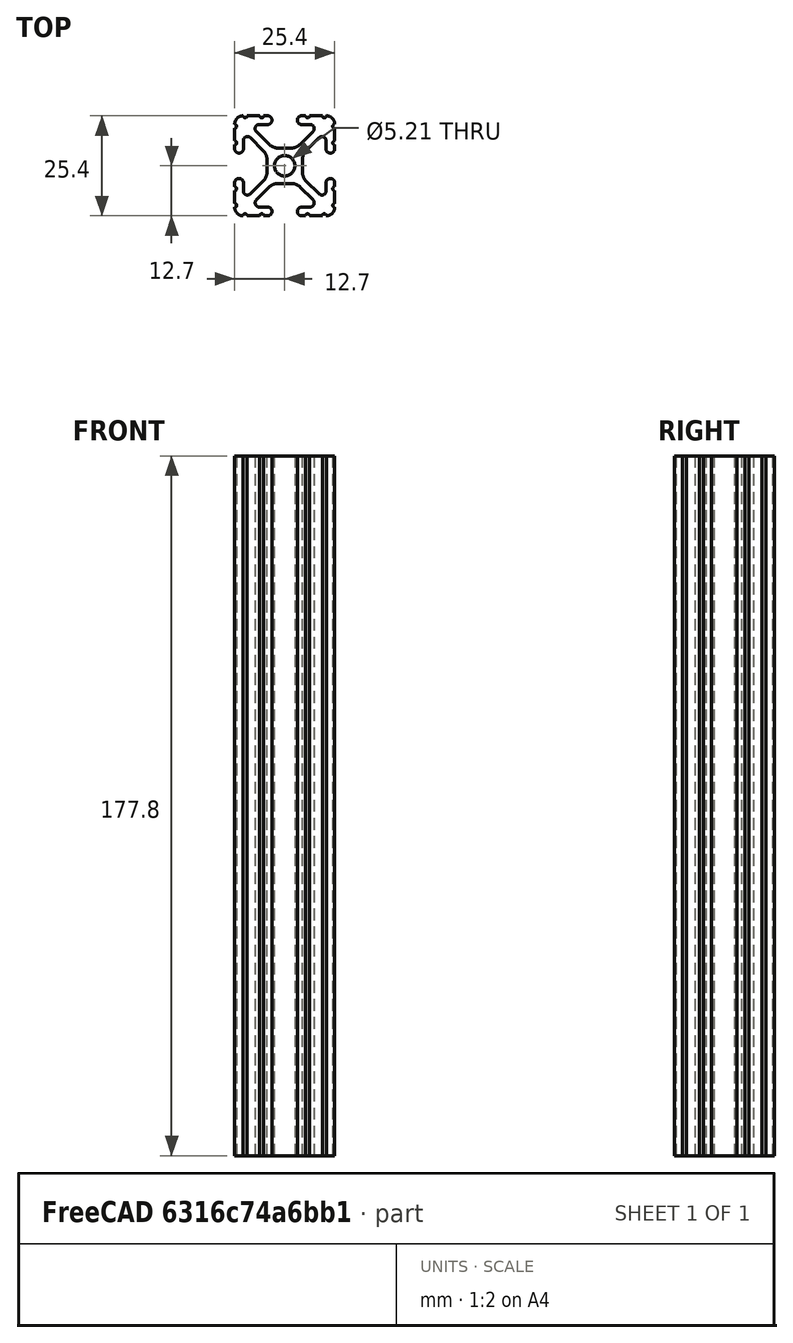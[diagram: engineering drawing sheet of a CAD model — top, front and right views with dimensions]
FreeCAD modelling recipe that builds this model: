
FCSTD DOCUMENT  (FreeCAD 0.19R23756 (Git))
Label: 1010-7
License: All rights reserved
LicenseURL: http://en.wikipedia.org/wiki/All_rights_reserved
objects: Sketcher::SketchObject×1, Part::Extrusion×1
note: 2 computed .brp shape members not serialized (recipe doc carries the construction recipe); baked Part::Feature solids carry a one-line shape summary decoded from their .brp

FEATURE [Sketcher::SketchObject] Sketch097
  FullyConstrained = false
  sketch-geometry (97):
    g0: Circle CenterX=0 CenterY=0 CenterZ=0 NormalX=0 NormalY=0 NormalZ=-1 AngleXU=0 Radius=2.6035
    g1: ArcOfCircle CenterX=12.7 CenterY=5.82508 CenterZ=0 NormalX=0 NormalY=0 NormalZ=1 AngleXU=0 Radius=0.508 StartAngle=1.5708 EndAngle=4.71239
    g2: LineSegment StartX=3.2385 StartY=11.651 StartZ=0 EndX=3.2385 EndY=11.5392 EndZ=0
    g3: LineSegment StartX=6.33313 StartY=-12.7 StartZ=0 EndX=9.55044 EndY=-12.7 EndZ=0
    g4: LineSegment StartX=7.20704 StartY=8.72437 StartZ=0 EndX=3.89827 EndY=5.42317 EndZ=0
    g5: ArcOfCircle CenterX=7.6835 CenterY=1.59319 CenterZ=0 NormalX=0 NormalY=0 NormalZ=1 AngleXU=0 Radius=3.175 StartAngle=2.35505 EndAngle=3.14159
    g6: ArcOfCircle CenterX=-1.70925 CenterY=-7.6708 CenterZ=0 NormalX=0 NormalY=0 NormalZ=1 AngleXU=0 Radius=3.175 StartAngle=1.5708 EndAngle=2.35528
    g7: ArcOfCircle CenterX=11.5392 CenterY=-4.28747 CenterZ=0 NormalX=0 NormalY=0 NormalZ=1 AngleXU=0 Radius=1.04901 StartAngle=1.5708 EndAngle=3.14159
    g8: ArcOfCircle CenterX=12.7 CenterY=-5.82508 CenterZ=0 NormalX=0 NormalY=0 NormalZ=1 AngleXU=0 Radius=0.508 StartAngle=1.5708 EndAngle=4.71239
    g9: LineSegment StartX=4.28751 StartY=10.4902 StartZ=0 EndX=6.47679 EndY=10.4902 EndZ=0
    g10: ArcOfCircle CenterX=4.28751 CenterY=11.651 CenterZ=0 NormalX=0 NormalY=0 NormalZ=1 AngleXU=0 Radius=1.04901 StartAngle=1.5708 EndAngle=3.14159
    g11: ArcOfCircle CenterX=6.47679 CenterY=9.45629 CenterZ=0 NormalX=0 NormalY=0 NormalZ=1 AngleXU=0 Radius=1.03391 StartAngle=5.49664 EndAngle=7.85398
    g12: ArcOfCircle CenterX=4.28751 CenterY=11.5392 CenterZ=0 NormalX=0 NormalY=0 NormalZ=1 AngleXU=0 Radius=1.04901 StartAngle=3.14159 EndAngle=4.71239
    g13: LineSegment StartX=3.95227 StartY=-5.42369 StartZ=0 EndX=7.17965 EndY=-8.64519 EndZ=0
    g14: ArcOfCircle CenterX=11.651 CenterY=4.28747 CenterZ=0 NormalX=0 NormalY=0 NormalZ=1 AngleXU=0 Radius=1.04901 StartAngle=4.71239 EndAngle=6.28319
    g15: ArcOfCircle CenterX=-5.82513 CenterY=-12.7 CenterZ=0 NormalX=0 NormalY=0 NormalZ=1 AngleXU=0 Radius=0.508 StartAngle=0 EndAngle=3.14159
    g16: LineSegment StartX=-6.47679 StartY=10.4902 StartZ=0 EndX=-4.28751 EndY=10.4902 EndZ=0
    g17: ArcOfCircle CenterX=-12.7 CenterY=10.0584 CenterZ=0 NormalX=0 NormalY=0 NormalZ=1 AngleXU=0 Radius=0.508 StartAngle=4.71239 EndAngle=7.85368
    g18: ArcOfCircle CenterX=-12.7 CenterY=5.82508 CenterZ=0 NormalX=0 NormalY=0 NormalZ=1 AngleXU=0 Radius=0.508 StartAngle=4.71239 EndAngle=7.85398
    g19: LineSegment StartX=-11.5392 StartY=-3.23846 StartZ=0 EndX=-11.651 EndY=-3.23846 EndZ=0
    g20: LineSegment StartX=-3.89827 StartY=5.42317 StartZ=0 EndX=-7.20704 EndY=8.72437 EndZ=0
    g21: LineSegment StartX=1.65578 StartY=4.4958 StartZ=0 EndX=-1.65578 EndY=4.4958 EndZ=0
    g22: ArcOfCircle CenterX=-1.65578 CenterY=7.6708 CenterZ=0 NormalX=0 NormalY=0 NormalZ=1 AngleXU=0 Radius=3.175 StartAngle=3.92813 EndAngle=4.71239
    g23: LineSegment StartX=-9.55044 StartY=-12.7 StartZ=0 EndX=-6.33313 EndY=-12.7 EndZ=0
    g24: ArcOfCircle CenterX=-5.82513 CenterY=12.7 CenterZ=0 NormalX=0 NormalY=0 NormalZ=1 AngleXU=0 Radius=0.508 StartAngle=3.14159 EndAngle=6.28319
    g25: ArcOfCircle CenterX=-4.28751 CenterY=11.651 CenterZ=0 NormalX=0 NormalY=0 NormalZ=1 AngleXU=0 Radius=1.04901 StartAngle=0 EndAngle=1.5708
    g26: LineSegment StartX=-12.7 StartY=-4.28747 StartZ=0 EndX=-12.7 EndY=-5.31708 EndZ=0
    g27: ArcOfCircle CenterX=-6.47679 CenterY=9.45629 CenterZ=0 NormalX=0 NormalY=0 NormalZ=1 AngleXU=0 Radius=1.03391 StartAngle=1.5708 EndAngle=3.92813
    g28: ArcOfCircle CenterX=-4.28751 CenterY=11.5392 CenterZ=0 NormalX=0 NormalY=0 NormalZ=1 AngleXU=0 Radius=1.04901 StartAngle=4.71239 EndAngle=6.28319
    g29: LineSegment StartX=-5.44101 StartY=-3.84082 StartZ=0 EndX=-8.73713 EndY=-7.12941 EndZ=0
    g30: ArcOfCircle CenterX=-7.6835 CenterY=-1.59319 CenterZ=0 NormalX=0 NormalY=0 NormalZ=1 AngleXU=0 Radius=3.175 StartAngle=5.49664 EndAngle=6.28319
    g31: LineSegment StartX=-12.7 StartY=5.31708 StartZ=0 EndX=-12.7 EndY=4.28747 EndZ=0
    g32: LineSegment StartX=-8.73713 StartY=7.12941 StartZ=0 EndX=-5.44101 EndY=3.84082 EndZ=0
    g33: LineSegment StartX=-11.651 StartY=3.23846 StartZ=0 EndX=-11.5392 EndY=3.23846 EndZ=0
    g34: ArcOfCircle CenterX=-9.46279 CenterY=-6.40209 CenterZ=0 NormalX=0 NormalY=0 NormalZ=1 AngleXU=0 Radius=1.02741 StartAngle=3.14159 EndAngle=5.49664
    g35: ArcOfCircle CenterX=-10.5918 CenterY=10.5918 CenterZ=0 NormalX=0 NormalY=0 NormalZ=1 AngleXU=0 Radius=2.1082 StartAngle=1.55877 EndAngle=3.15364
    g36: LineSegment StartX=-12.7 StartY=9.5504 StartZ=0 EndX=-12.7 EndY=6.33308 EndZ=0
    g37: LineSegment StartX=-6.33313 StartY=12.7 StartZ=0 EndX=-9.55044 EndY=12.7 EndZ=0
    g38: ArcOfCircle CenterX=-11.5392 CenterY=-4.28747 CenterZ=0 NormalX=0 NormalY=0 NormalZ=1 AngleXU=0 Radius=1.04901 StartAngle=0 EndAngle=1.5708
    g39: LineSegment StartX=4.28751 StartY=-12.7 StartZ=0 EndX=5.31713 EndY=-12.7 EndZ=0
    g40: LineSegment StartX=5.44101 StartY=3.84082 StartZ=0 EndX=8.73713 EndY=7.12941 EndZ=0
    g41: LineSegment StartX=10.4902 StartY=-4.28747 StartZ=0 EndX=10.4902 EndY=-6.40209 EndZ=0
    g42: ArcOfCircle CenterX=9.46279 CenterY=6.40209 CenterZ=0 NormalX=0 NormalY=0 NormalZ=1 AngleXU=0 Radius=1.02741 StartAngle=0 EndAngle=2.35505
    g43: ArcOfCircle CenterX=5.82513 CenterY=-12.7 CenterZ=0 NormalX=0 NormalY=0 NormalZ=1 AngleXU=0 Radius=0.508 StartAngle=0 EndAngle=3.14159
    g44: LineSegment StartX=12.7 StartY=-9.5504 StartZ=0 EndX=12.7 EndY=-6.33308 EndZ=0
    g45: LineSegment StartX=4.5085 StartY=-1.59319 StartZ=0 EndX=4.5085 EndY=1.59319 EndZ=0
    g46: ArcOfCircle CenterX=12.7 CenterY=10.0584 CenterZ=0 NormalX=0 NormalY=0 NormalZ=1 AngleXU=0 Radius=0.508 StartAngle=1.5711 EndAngle=4.71239
    g47: ArcOfCircle CenterX=12.7 CenterY=-10.0584 CenterZ=0 NormalX=0 NormalY=0 NormalZ=1 AngleXU=0 Radius=0.508 StartAngle=1.5708 EndAngle=4.71209
    g48: LineSegment StartX=3.2385 StartY=-11.5392 StartZ=0 EndX=3.2385 EndY=-11.651 EndZ=0
    g49: LineSegment StartX=8.73713 StartY=-7.12941 StartZ=0 EndX=5.44101 EndY=-3.84082 EndZ=0
    g50: ArcOfCircle CenterX=11.651 CenterY=-4.28747 CenterZ=0 NormalX=0 NormalY=0 NormalZ=1 AngleXU=0 Radius=1.04901 StartAngle=0 EndAngle=1.5708
    g51: ArcOfCircle CenterX=1.65578 CenterY=7.6708 CenterZ=0 NormalX=0 NormalY=0 NormalZ=1 AngleXU=0 Radius=3.175 StartAngle=4.71239 EndAngle=5.49664
    g52: ArcOfCircle CenterX=7.6835 CenterY=-1.59319 CenterZ=0 NormalX=0 NormalY=0 NormalZ=1 AngleXU=0 Radius=3.175 StartAngle=3.14159 EndAngle=3.92813
    g53: LineSegment StartX=12.7 StartY=4.28747 StartZ=0 EndX=12.7 EndY=5.31708 EndZ=0
    g54: ArcOfCircle CenterX=6.41641 CenterY=-9.40983 CenterZ=0 NormalX=0 NormalY=0 NormalZ=1 AngleXU=0 Radius=1.08037 StartAngle=4.71239 EndAngle=7.06949
    g55: LineSegment StartX=12.7 StartY=-5.31708 StartZ=0 EndX=12.7 EndY=-4.28747 EndZ=0
    g56: ArcOfCircle CenterX=10.0584 CenterY=-12.7 CenterZ=0 NormalX=0 NormalY=0 NormalZ=1 AngleXU=0 Radius=0.508 StartAngle=0.000300194 EndAngle=3.14159
    g57: ArcOfCircle CenterX=11.5392 CenterY=4.28747 CenterZ=0 NormalX=0 NormalY=0 NormalZ=1 AngleXU=0 Radius=1.04901 StartAngle=3.14159 EndAngle=4.71239
    g58: LineSegment StartX=12.7 StartY=6.33308 StartZ=0 EndX=12.7 EndY=9.5504 EndZ=0
    g59: ArcOfCircle CenterX=4.28751 CenterY=-11.5392 CenterZ=0 NormalX=0 NormalY=0 NormalZ=1 AngleXU=0 Radius=1.04901 StartAngle=1.5708 EndAngle=3.14159
    g60: ArcOfCircle CenterX=10.5918 CenterY=10.5918 CenterZ=0 NormalX=0 NormalY=0 NormalZ=1 AngleXU=0 Radius=2.1082 StartAngle=6.27114 EndAngle=7.86601
    g61: ArcOfCircle CenterX=9.46279 CenterY=-6.40209 CenterZ=0 NormalX=0 NormalY=0 NormalZ=1 AngleXU=0 Radius=1.02741 StartAngle=3.92813 EndAngle=6.28319
    g62: LineSegment StartX=6.41641 StartY=-10.4902 StartZ=0 EndX=4.28751 EndY=-10.4902 EndZ=0
    g63: LineSegment StartX=-10.4902 StartY=-6.40209 StartZ=0 EndX=-10.4902 EndY=-4.28747 EndZ=0
    g64: ArcOfCircle CenterX=-9.46279 CenterY=6.40209 CenterZ=0 NormalX=0 NormalY=0 NormalZ=1 AngleXU=0 Radius=1.02741 StartAngle=0.786542 EndAngle=3.14159
    g65: LineSegment StartX=-10.4902 StartY=4.28747 StartZ=0 EndX=-10.4902 EndY=6.40209 EndZ=0
    g66: LineSegment StartX=-4.5085 StartY=1.59319 StartZ=0 EndX=-4.5085 EndY=-1.59319 EndZ=0
    g67: LineSegment StartX=-4.28751 StartY=12.7 StartZ=0 EndX=-5.31713 EndY=12.7 EndZ=0
    g68: ArcOfCircle CenterX=-11.5392 CenterY=4.28747 CenterZ=0 NormalX=0 NormalY=0 NormalZ=1 AngleXU=0 Radius=1.04901 StartAngle=4.71239 EndAngle=6.28319
    g69: LineSegment StartX=-3.2385 StartY=11.5392 StartZ=0 EndX=-3.2385 EndY=11.651 EndZ=0
    g70: ArcOfCircle CenterX=-11.651 CenterY=4.28747 CenterZ=0 NormalX=0 NormalY=0 NormalZ=1 AngleXU=0 Radius=1.04901 StartAngle=3.14159 EndAngle=4.71239
    g71: ArcOfCircle CenterX=-7.6835 CenterY=1.59319 CenterZ=0 NormalX=0 NormalY=0 NormalZ=1 AngleXU=0 Radius=3.175 StartAngle=0 EndAngle=0.786542
    g72: ArcOfCircle CenterX=-10.0584 CenterY=12.7 CenterZ=0 NormalX=0 NormalY=0 NormalZ=1 AngleXU=0 Radius=0.508 StartAngle=3.14189 EndAngle=6.28319
    g73: LineSegment StartX=-1.70925 StartY=-4.4958 StartZ=0 EndX=1.70925 EndY=-4.4958 EndZ=0
    g74: LineSegment StartX=11.651 StartY=-3.23846 StartZ=0 EndX=11.5392 EndY=-3.23846 EndZ=0
    g75: ArcOfCircle CenterX=-10.5918 CenterY=-10.5918 CenterZ=0 NormalX=0 NormalY=0 NormalZ=1 AngleXU=0 Radius=2.1082 StartAngle=3.12954 EndAngle=4.72442
    g76: ArcOfCircle CenterX=10.5918 CenterY=-10.5918 CenterZ=0 NormalX=0 NormalY=0 NormalZ=1 AngleXU=0 Radius=2.1082 StartAngle=4.70036 EndAngle=6.29523
    g77: ArcOfCircle CenterX=-12.7 CenterY=-5.82508 CenterZ=0 NormalX=0 NormalY=0 NormalZ=1 AngleXU=0 Radius=0.508 StartAngle=4.71239 EndAngle=7.85398
    g78: ArcOfCircle CenterX=5.82513 CenterY=12.7 CenterZ=0 NormalX=0 NormalY=0 NormalZ=1 AngleXU=0 Radius=0.508 StartAngle=3.14159 EndAngle=6.28319
    g79: LineSegment StartX=9.55044 StartY=12.7 StartZ=0 EndX=6.33313 EndY=12.7 EndZ=0
    g80: ArcOfCircle CenterX=10.0584 CenterY=12.7 CenterZ=0 NormalX=0 NormalY=0 NormalZ=1 AngleXU=0 Radius=0.508 StartAngle=3.14159 EndAngle=6.28289
    g81: ArcOfCircle CenterX=1.70925 CenterY=-7.6708 CenterZ=0 NormalX=0 NormalY=0 NormalZ=1 AngleXU=0 Radius=3.175 StartAngle=0.78631 EndAngle=1.5708
    g82: ArcOfCircle CenterX=4.28751 CenterY=-11.651 CenterZ=0 NormalX=0 NormalY=0 NormalZ=1 AngleXU=0 Radius=1.04901 StartAngle=3.14159 EndAngle=4.71239
    g83: LineSegment StartX=5.31713 StartY=12.7 StartZ=0 EndX=4.28751 EndY=12.7 EndZ=0
    g84: LineSegment StartX=10.4902 StartY=6.40209 StartZ=0 EndX=10.4902 EndY=4.28747 EndZ=0
    g85: LineSegment StartX=11.5392 StartY=3.23846 StartZ=0 EndX=11.651 EndY=3.23846 EndZ=0
    g86: ArcOfCircle CenterX=-10.0584 CenterY=-12.7 CenterZ=0 NormalX=0 NormalY=0 NormalZ=1 AngleXU=0 Radius=0.508 StartAngle=0 EndAngle=3.14129
    g87: ArcOfCircle CenterX=-12.7 CenterY=-10.0584 CenterZ=0 NormalX=0 NormalY=0 NormalZ=1 AngleXU=0 Radius=0.508 StartAngle=4.71269 EndAngle=7.85398
    g88: ArcOfCircle CenterX=-4.28751 CenterY=-11.5392 CenterZ=0 NormalX=0 NormalY=0 NormalZ=1 AngleXU=0 Radius=1.04901 StartAngle=0 EndAngle=1.5708
    g89: ArcOfCircle CenterX=-4.28751 CenterY=-11.651 CenterZ=0 NormalX=0 NormalY=0 NormalZ=1 AngleXU=0 Radius=1.04901 StartAngle=4.71239 EndAngle=6.28319
    g90: LineSegment StartX=-12.7 StartY=-6.33308 StartZ=0 EndX=-12.7 EndY=-9.5504 EndZ=0
    g91: ArcOfCircle CenterX=-11.651 CenterY=-4.28747 CenterZ=0 NormalX=0 NormalY=0 NormalZ=1 AngleXU=0 Radius=1.04901 StartAngle=1.5708 EndAngle=3.14159
    g92: LineSegment StartX=-7.17965 StartY=-8.64519 StartZ=0 EndX=-3.95227 EndY=-5.42369 EndZ=0
    g93: LineSegment StartX=-5.31713 StartY=-12.7 StartZ=0 EndX=-4.28751 EndY=-12.7 EndZ=0
    g94: LineSegment StartX=-3.2385 StartY=-11.651 StartZ=0 EndX=-3.2385 EndY=-11.5392 EndZ=0
    g95: ArcOfCircle CenterX=-6.41641 CenterY=-9.40983 CenterZ=0 NormalX=0 NormalY=0 NormalZ=1 AngleXU=0 Radius=1.08037 StartAngle=2.35528 EndAngle=4.71239
    g96: LineSegment StartX=-4.28751 StartY=-10.4902 StartZ=0 EndX=-6.41641 EndY=-10.4902 EndZ=0
FEATURE [Part::Extrusion] Extrude
  Base = -> Sketch097
  Dir = (0,0,1)
  DirMode = 2
  FaceMakerClass = Part::FaceMakerBullseye
  LengthFwd = 177.8
  LengthRev = 0
  Solid = true
  Symmetric = false
